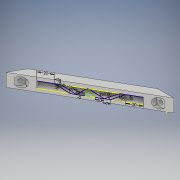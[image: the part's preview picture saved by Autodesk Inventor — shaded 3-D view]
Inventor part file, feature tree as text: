
AUTODESK INVENTOR PART (.ipt)
format: ipt  version: 2019.4 (Build 234330000, 330)  size: 215,552 bytes
history: native  units: mm
features: sketch x9, extrude x8, plane x3
ambient origin geometry x8: Origin, YZ Plane, XZ Plane, XY Plane, X Axis, Y Axis, Z Axis, Center Point
bodies: Solid1 (feature_tree)
feature tree (20):
  extrude  "Extrusion1"  TaperAngle=0.0deg  [1 undecoded]
  plane  "Work Plane1"
  plane  "Work Plane3"
  extrude  "Extrusion6"  TaperAngle=120.0deg  [1 undecoded]
  plane  "Work Plane4"
  extrude  "Extrusion7"  Depth=10.0mm
  extrude  "Extrusion8"  Depth=10.0mm
  extrude  "Extrusion9"  Depth=10.0mm
  extrude  "Extrusion10"  Depth=20.0mm TaperAngle=0.0deg
  extrude  "Extrusion11"  [1 undecoded]
  extrude  "Extrusion12"  Depth=5.0mm
  sketch  "Sketch14"  dims[d40=5.0mm d41=5.0mm d42=10.0mm d43=0.0mm d44=-5.0mm d45=5.0mm d46=5.0mm d47=5.0mm d48=90.0deg d49=5.0mm d50=10.0mm d51=0.0mm d52=15.0mm d53=10.0mm d54=0.0mm d55=5.5mm d56=5.0mm d57=0.0mm d58=90.0deg d59=15.0mm d60=10.0mm d61=0.0mm d62=5.5mm d63=5.0mm d64=0.0mm d65=60.0mm d66=5.0mm d67=60.0mm d68=5.0mm d69=15.0mm d70=0.0mm d71=20.0mm d72=20.0mm d73=30.0deg d74=150.0deg d75=7.0mm d76=7.0mm d77=7.0mm d78=7.0mm d79=6.981317mm d80=150.0deg d81=10.0mm d82=10.0mm]
  sketch  "Sketch1"  dims[d2=100.0mm d3=0.0mm]
  sketch  "Sketch7"  dims[d4=100.0mm d5=120.0deg]
  sketch  "Sketch8"  dims[d6=10.0mm d7=10.0mm]
  sketch  "Sketch9"  dims[d8=150.0deg d9=10.0mm]
  sketch  "Sketch10"  dims[d10=15.0mm d11=10.0mm]
  sketch  "Sketch11"  dims[d12=15.0mm d13=20.0mm d14=0.0mm]
  sketch  "Sketch12"  dims[d19=15.0mm d37=-5.0mm]
  sketch  "Sketch13"  dims[d38=5.0mm d39=5.0mm]
note: 3 required parameter values undecoded (feature->parameter linkage not recoverable at this tier; creation-order binding heuristic only, values carry confidence <= 0.55)
